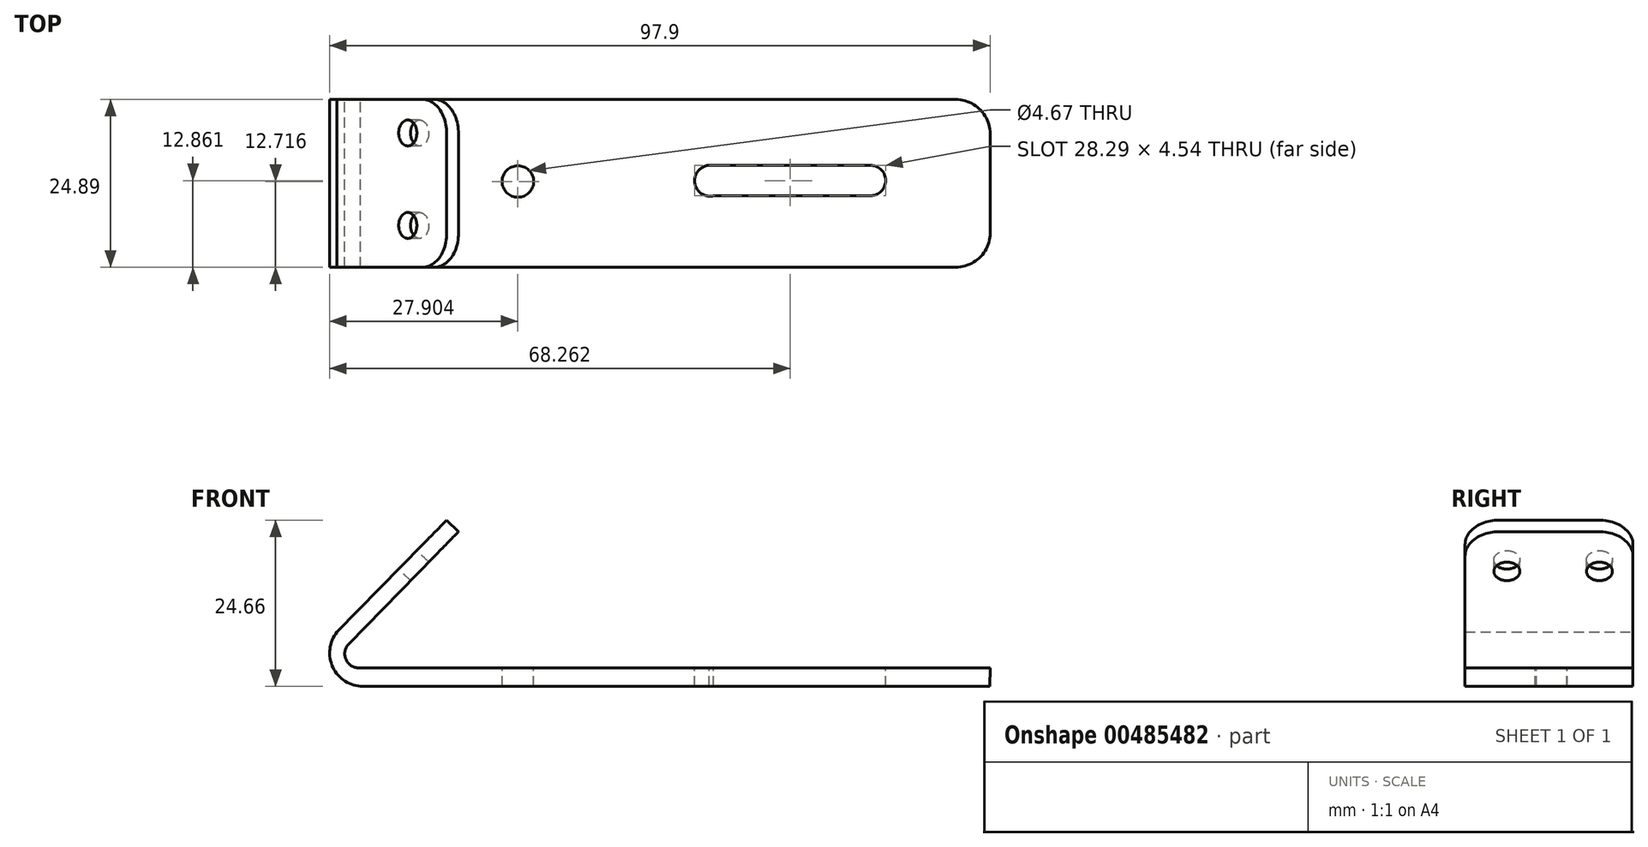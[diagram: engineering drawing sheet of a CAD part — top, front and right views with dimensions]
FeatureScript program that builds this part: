
annotation { "Feature Type Name" : "Feature", "Feature Type Description" : "" }
export const myFeature = defineFeature(function(context is Context, id is Id, definition is map)
    precondition{}
    {
        {
            var Q0;
            Q0=qCreatedBy(makeId("Front.planeOp"),FACE);
            var sketch = newSketch(context, id + "F0", { "sketchPlane" : qUnion([Q0])});
            skLineSegment(sketch, "E0", {"start": v(50.74, 7.4) * mm, "end": v(-42.17, 7.4) * mm});
            skArc(sketch, "E1", {"start": v(-42.17, 7.4) * mm, "mid": v(-46.63, 10.22) * mm, "end": v(-46.01, 15.45) * mm});
            skLineSegment(sketch, "E2", {"start": v(-46.01, 15.45) * mm, "end": v(-29.76, 32.07) * mm});
            skLineSegment(sketch, "E3", {"start": v(-29.76, 32.07) * mm, "end": v(-28, 30.36) * mm});
            skLineSegment(sketch, "E4", {"start": v(-28, 30.36) * mm, "end": v(-44.28, 13.71) * mm});
            skArc(sketch, "E5", {"start": v(-44.28, 13.71) * mm, "mid": v(-44.66, 11.32) * mm, "end": v(-42.54, 10.16) * mm});
            skLineSegment(sketch, "E6", {"start": v(-42.54, 10.16) * mm, "end": v(50.79, 10.16) * mm});
            skLineSegment(sketch, "E7", {"start": v(50.79, 10.16) * mm, "end": v(50.74, 7.4) * mm});
            skSolve(sketch);
        }
        {
            var Q0;
            Q0=makeQuery(id+"F0.imprint","IMPRINT",FACE,{"disambiguationData":[TD([[makeQuery(id+"F0.imprint","IMPRINT",EDGE,{"derivedFrom":sQuery(id+"F0.wireOp",EDGE,"E0")}),-1.0]])]});
            extrude(context, id + "F1", {"entities" : qUnion([Q0]), "depth" : 24.9 * mm});
        }
        {
            var Q0;
            Q0=makeQuery(id+"F1.opExtrude","SWEPT_FACE",FACE,{"disambiguationData":[OSD([sQuery(id+"F0.wireOp",EDGE,"E2")])]});
            cPlane(context, id + "F2", {"entities" : qUnion([Q0]), "cplaneType" : CPlaneType.OFFSET, "offset" : 5.33 * mm, "width" : 152.4 * mm, "height" : 152.4 * mm});
        }
        {
            var Q0;
            Q0=qCreatedBy(id+"F2.planeOp",FACE);
            var sketch = newSketch(context, id + "F3", { "sketchPlane" : qUnion([Q0])});
            skCircle(sketch, "E8", {"center": v(4.97, -6.13) * mm, "radius": 1.92 * mm});
            skCircle(sketch, "E9.1.0.0", {"center": v(18.69, -6.13) * mm, "radius": 1.92 * mm});
            skLineSegment(sketch, "E9.direction1", {"start": v(4.97, -6.13) * mm, "end": v(18.69, -6.13) * mm, "construction": true});
            skSolve(sketch);
        }
        {
            var Q0;
            Q0 = qSketchRegion(id + "F3", true);
            extrude(context, id + "F4", {"entities" : qUnion([Q0]), "operationType" : NewBodyOperationType.REMOVE, "oppositeDirection" : true, "depth" : 25.4 * mm});
        }
        {
            var Q0;
            Q0=qCreatedBy(makeId("Top.planeOp"),FACE);
            cPlane(context, id + "F5", {"entities" : qUnion([Q0]), "cplaneType" : CPlaneType.OFFSET, "offset" : 17.78 * mm, "width" : 152.4 * mm, "height" : 152.4 * mm});
        }
        {
            var Q0;
            Q0=qCreatedBy(id+"F5.planeOp",FACE);
            var sketch = newSketch(context, id + "F6", { "sketchPlane" : qUnion([Q0])});
            skCircle(sketch, "E10", {"center": v(-19.2, -12.17) * mm, "radius": 2.34 * mm});
            skSolve(sketch);
        }
        {
            var Q0;
            Q0=qCreatedBy(id+"F5.planeOp",FACE);
            var sketch = newSketch(context, id + "F7", { "sketchPlane" : qUnion([Q0])});
            skCircle(sketch, "E11", {"center": v(9.28, -12.05) * mm, "radius": 2.3 * mm});
            skLineSegment(sketch, "E12.bottom", {"start": v(9.16, -9.76) * mm, "end": v(33.03, -9.76) * mm});
            skLineSegment(sketch, "E12.top", {"start": v(9.16, -14.29) * mm, "end": v(33.03, -14.29) * mm});
            skLineSegment(sketch, "E12.left", {"start": v(9.16, -9.76) * mm, "end": v(9.16, -14.29) * mm});
            skLineSegment(sketch, "E12.right", {"start": v(33.03, -9.76) * mm, "end": v(33.03, -14.29) * mm});
            skCircle(sketch, "E13", {"center": v(33.03, -12.02) * mm, "radius": 2.26 * mm});
            skSolve(sketch);
        }
        {
            var Q0;
            {var subQ0=sQuery(id+"F7.wireOp",EDGE,"E12.bottom");var subQ1=sQuery(id+"F7.wireOp",EDGE,"E11");var subQ2=makeQuery(id+"F7.imprint","INTERSECT",VERTEX,{"derivedFrom":[subQ1,subQ0]});Q0=makeQuery(id+"F7.imprint","IMPRINT",FACE,{"disambiguationData":[TD([[makeQuery(id+"F7.imprint","IMPRINT",EDGE,{"disambiguationData":[TD([[subQ2,1.0]])],"derivedFrom":subQ1}),-1.0]])]});}
            var Q1;
            {var subQ0=sQuery(id+"F7.wireOp",EDGE,"E12.right");Q1=makeQuery(id+"F7.imprint","IMPRINT",FACE,{"disambiguationData":[TD([[makeQuery(id+"F7.imprint","IMPRINT",EDGE,{"derivedFrom":subQ0}),-1.0]])]});}
            var Q2;
            {var subQ0=sQuery(id+"F7.wireOp",EDGE,"E12.right");Q2=makeQuery(id+"F7.imprint","IMPRINT",FACE,{"disambiguationData":[TD([[makeQuery(id+"F7.imprint","IMPRINT",EDGE,{"derivedFrom":subQ0}),1.0]])]});}
            var Q3;
            {var subQ0=sQuery(id+"F7.wireOp",EDGE,"E12.left");Q3=makeQuery(id+"F7.imprint","IMPRINT",FACE,{"disambiguationData":[TD([[makeQuery(id+"F7.imprint","IMPRINT",EDGE,{"derivedFrom":subQ0}),-1.0]])]});}
            var Q4;
            {var subQ5=sQuery(id+"F7.wireOp",EDGE,"E12.left");Q4=makeQuery(id+"F7.imprint","IMPRINT",FACE,{"disambiguationData":[TD([[makeQuery(id+"F7.imprint","IMPRINT",EDGE,{"derivedFrom":subQ5}),1.0]])]});}
            extrude(context, id + "F8", {"entities" : qUnion([Q0, Q1, Q2, Q3, Q4]), "operationType" : NewBodyOperationType.REMOVE, "oppositeDirection" : true, "depth" : 25.4 * mm});
        }
        {
            var Q0;
            Q0=makeQuery(id+"F6.imprint","IMPRINT",FACE,{"disambiguationData":[TD([[makeQuery(id+"F6.imprint","IMPRINT",EDGE,{"derivedFrom":sQuery(id+"F6.wireOp",EDGE,"E10")}),1.0]])]});
            extrude(context, id + "F9", {"entities" : qUnion([Q0]), "operationType" : NewBodyOperationType.REMOVE, "oppositeDirection" : true, "depth" : 25.4 * mm});
        }
        {
            var Q0;
            Q0=makeQuery(id+"F1.opExtrude","CAP_EDGE",EDGE,{"disambiguationData":[OSD([sQuery(id+"F0.wireOp",EDGE,"E3")])],"isStart":true});
            var Q1;
            Q1=makeQuery(id+"F1.opExtrude","CAP_EDGE",EDGE,{"disambiguationData":[OSD([sQuery(id+"F0.wireOp",EDGE,"E3")])],"isStart":false});
            var Q2;
            Q2=makeQuery(id+"F1.opExtrude","CAP_EDGE",EDGE,{"disambiguationData":[OSD([sQuery(id+"F0.wireOp",EDGE,"E7")])],"isStart":false});
            var Q3;
            Q3=makeQuery(id+"F1.opExtrude","CAP_EDGE",EDGE,{"disambiguationData":[OSD([sQuery(id+"F0.wireOp",EDGE,"E7")])],"isStart":true});
            fillet(context, id + "F10", {"entities" : qUnion([Q0, Q1, Q2, Q3]), "radius" : 5.08 * mm, "tangentPropagation" : true, "allowEdgeOverflow" : false});
        }
    });
